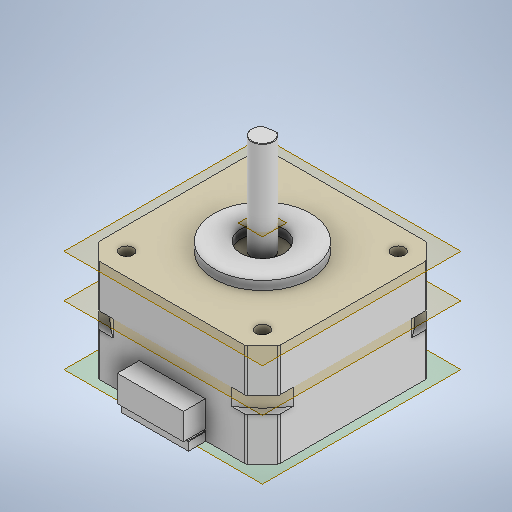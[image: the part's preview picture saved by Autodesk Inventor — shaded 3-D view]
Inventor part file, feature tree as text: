
AUTODESK INVENTOR PART (.ipt)
format: ipt  version: 2025.1 (Build 291241000, 241)  size: 428,544 bytes
history: native  units: mm
features: sketch x10, extrude x8, other x6, fillet x2, hole x2
ambient origin geometry x8: Origin, YZ Plane, XZ Plane, XY Plane, X Axis, Y Axis, Z Axis, Center Point
bodies: Body1 (feature_tree)
feature tree (28):
  other  "ソリッド1"
  extrude  "押し出し1"  Depth=5.4mm
  extrude  "押し出し2"  Depth=5.4mm
  other  "作業平面1"
  extrude  "押し出し3"  Depth=0.6mm
  other  "作業平面2"
  extrude  "押し出し4"  Depth=9.8mm TaperAngle=0.0deg
  fillet  "フィレット1"  Radius=10.0mm
  other  "作業平面3"
  hole  "穴1"  [1 undecoded]
  extrude  "押し出し5"  Depth=3.8mm TaperAngle=0.0deg
  extrude  "押し出し6"  TaperAngle=0.0deg  [1 undecoded]
  other  "作業平面4"
  extrude  "押し出し7"  Depth=41.2mm
  fillet  "フィレット2"  Radius=41.2mm
  other  "作業平面5"
  extrude  "押し出し8"  Depth=0.6mm
  hole  "穴2"  [1 undecoded]
  sketch  "スケッチ1"
  sketch  "スケッチ2"
  sketch  "スケッチ4"
  sketch  "スケッチ5"
  sketch  "スケッチ6"
  sketch  "スケッチ7"
  sketch  "スケッチ8"
  sketch  "スケッチ9"
  sketch  "スケッチ10"
  sketch  "スケッチ11"
note: 3 required parameter values undecoded (feature->parameter linkage not recoverable at this tier; creation-order binding heuristic only, values carry confidence <= 0.55)
